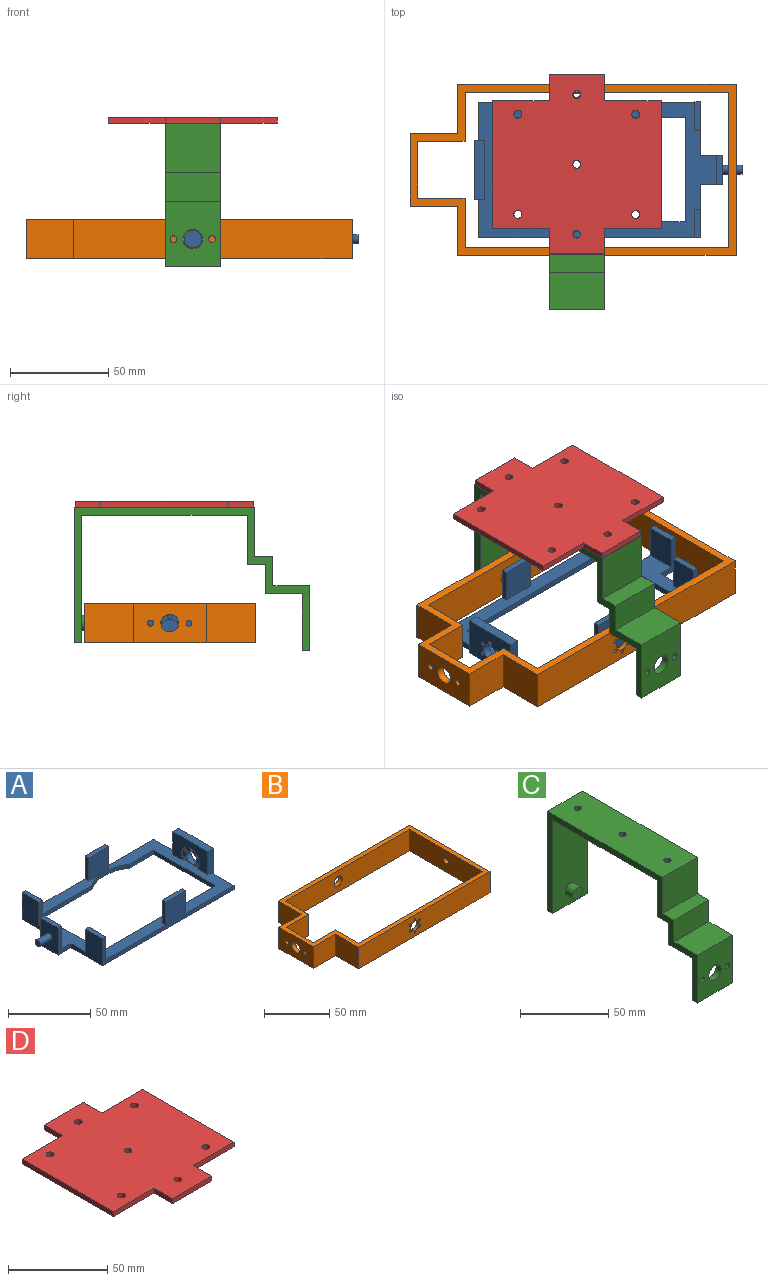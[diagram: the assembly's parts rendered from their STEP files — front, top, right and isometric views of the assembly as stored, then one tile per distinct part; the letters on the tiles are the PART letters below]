
ASSEMBLY  parts=4 mates=1
PART A: 48 faces, bbox 136x69x20 mm
  f0: cylinder r=4.5mm len=9mm, axis (1,0,0), area 113.1mm2, adj f43,f44
  f1: cylinder r=1mm len=4mm, axis (1,0,0), area 25.1mm2, adj f43,f44
  f2: cylinder r=1mm len=4mm, axis (1,0,0), area 25.1mm2, adj f43,f44
  f3: cylinder r=1mm len=4mm, axis (1,0,0), area 25.1mm2, adj f43,f44
  f4: cylinder r=1mm len=4mm, axis (1,0,0), area 25.1mm2, adj f43,f44
  f5: cylinder r=1mm len=4mm, axis (1,0,0), area 25.1mm2, adj f43,f44
  f6: plane 19.5x3mm, normal (1,0,0), area 58.5mm2, adj f7,f9,f24,f33
  f7: plane 121x69mm, normal (0,0,1), area 2401mm2, adj f6,f8,f9,f10,f11,f12,f13,f14
  f8: plane 27x20mm, normal (-1,0,0), area 327.5mm2, adj f7,f9,f18,f24,f36,f38
  f9: plane 113x20mm, normal (0,1,0), area 679mm2, adj f6,f7,f8,f16,f18,f22,f24,f32
  f10: plane 27x20mm, normal (-1,0,0), area 327.5mm2, adj f7,f11,f19,f24,f37,f39
  f11: plane 113x20mm, normal (0,-1,0), area 679mm2, adj f7,f10,f12,f17,f19,f23,f24,f31
  f12: plane 17x14.5mm, normal (1,0,0), area 246.5mm2, adj f7,f11,f19,f37
  f13: plane 17x17mm, normal (0,-1,0), area 289mm2, adj f7,f16,f32,f35
  f14: plane 30x17mm, normal (-1,0,0), area 352.1mm2, adj f7,f20,f30,f33,f45
  f15: plane 17x17mm, normal (0,1,0), area 289mm2, adj f7,f17,f31,f34
  f16: plane 17x3mm, normal (0,0,1), area 51mm2, adj f9,f13,f32,f35
  f17: plane 17x3mm, normal (0,0,1), area 51mm2, adj f11,f15,f31,f34
  f18: plane 14.5x3mm, normal (0,0,1), area 43.5mm2, adj f8,f9,f22,f36
  f19: plane 14.5x3mm, normal (0,0,1), area 43.5mm2, adj f10,f11,f12,f37
  f20: plane 30x5mm, normal (0,0,1), area 150mm2, adj f14,f30,f33,f43
  f21: plane 21.03x3mm, normal (0,-1,0), area 63.1mm2, adj f7,f24,f28,f29
  f22: plane 17x14.5mm, normal (1,0,0), area 246.5mm2, adj f7,f9,f18,f36
  f23: plane 19.5x3mm, normal (1,0,0), area 58.5mm2, adj f7,f11,f24,f30
  f24: plane 126x69mm, normal (0,0,-1), area 2772.5mm2, adj f6,f8,f9,f10,f11,f21,f23,f25
  f25: plane 44.03x3mm, normal (0,-1,0), area 132.1mm2, adj f7,f24,f26,f29
  f26: plane 53x3mm, normal (1,0,0), area 159mm2, adj f7,f24,f25,f27
  f27: plane 97x3mm, normal (0,1,0), area 291mm2, adj f7,f24,f26,f28
  f28: plane 53x3mm, normal (-1,0,0), area 159mm2, adj f7,f21,f24,f27
  f29: cylinder r=28mm len=31.94mm, axis (0,0,1), area 102mm2, adj f7,f21,f24,f25
  f30: plane 20x5mm, normal (0,-1,0), area 91mm2, adj f7,f14,f20,f23,f24,f43
  f31: plane 17x3mm, normal (1,0,0), area 51mm2, adj f7,f11,f15,f17
  f32: plane 17x3mm, normal (1,0,0), area 51mm2, adj f7,f9,f13,f16
  f33: plane 20x5mm, normal (0,1,0), area 91mm2, adj f6,f7,f14,f20,f24,f43
  f34: plane 17x3mm, normal (-1,0,0), area 51mm2, adj f7,f11,f15,f17
  f35: plane 17x3mm, normal (-1,0,0), area 51mm2, adj f7,f9,f13,f16
  f36: plane 17x3mm, normal (0,-1,0), area 51mm2, adj f7,f8,f18,f22
  f37: plane 17x3mm, normal (0,1,0), area 51mm2, adj f7,f10,f12,f19
  f38: plane 20x11mm, normal (0,1,0), area 84mm2, adj f7,f8,f24,f40,f41,f42
  f39: plane 20x11mm, normal (0,-1,0), area 84mm2, adj f7,f10,f24,f40,f41,f42
  f40: plane 20x15mm, normal (-1,0,0), area 283.4mm2, adj f24,f38,f39,f41,f46
  f41: plane 15x3mm, normal (0,0,1), area 45mm2, adj f38,f39,f40,f42
  f42: plane 17x15mm, normal (1,0,0), area 255mm2, adj f7,f38,f39,f41
  f43: plane 30x20mm, normal (1,0,0), area 520.7mm2, adj f0,f1,f2,f3,f4,f5,f20,f24
  f44: plane 15.38x12.19mm, normal (-1,0,0), area 78.6mm2, adj f0,f1,f2,f3,f4,f5,f7,f45
  f45: cylinder r=7.69mm len=15.38mm, axis (-1,0,0), area 33.8mm2, adj f7,f14,f44
  f46: cylinder r=2.3mm len=10mm, axis (1,0,0), area 144.5mm2, adj f40,f47
  f47: plane 4.6x4.6mm, normal (-1,0,0), area 16.6mm2, adj f46
PART B: 36 faces, bbox 166x87x20 mm
  f0: cylinder r=4.5mm len=9mm, axis (0,1,0), area 70.7mm2, adj f16,f34
  f1: cylinder r=1mm len=2.5mm, axis (0,-1,0), area 15.7mm2, adj f16,f34
  f2: cylinder r=1mm len=2.5mm, axis (0,-1,0), area 15.7mm2, adj f16,f34
  f3: cylinder r=1mm len=2.5mm, axis (0,-1,0), area 15.7mm2, adj f16,f34
  f4: cylinder r=1mm len=2.5mm, axis (0,-1,0), area 15.7mm2, adj f16,f34
  f5: cylinder r=1mm len=2.5mm, axis (0,-1,0), area 15.7mm2, adj f16,f34
  f6: cylinder r=1mm len=2.5mm, axis (0,-1,0), area 15.7mm2, adj f16,f34
  f7: plane 29x20mm, normal (1,0,0), area 473.9mm2, adj f17,f23,f25,f26,f29,f30,f33
  f8: cylinder r=1.5mm len=3mm, axis (1,0,0), area 23.6mm2, adj f10,f32
  f9: cylinder r=1.5mm len=3mm, axis (1,0,0), area 23.6mm2, adj f10,f31
  f10: plane 37x20mm, normal (-1,0,0), area 662.2mm2, adj f8,f9,f13,f14,f25,f26,f29
  f11: plane 142x20mm, normal (0,1,0), area 2776.4mm2, adj f12,f24,f25,f26,f28
  f12: plane 25x20mm, normal (-1,0,0), area 500mm2, adj f11,f13,f25,f26
  f13: plane 24x20mm, normal (0,1,0), area 480mm2, adj f10,f12,f25,f26
  f14: plane 24x20mm, normal (0,-1,0), area 480mm2, adj f10,f15,f25,f26
  f15: plane 25x20mm, normal (-1,0,0), area 500mm2, adj f14,f16,f25,f26
  f16: plane 142x20mm, normal (0,-1,0), area 2757.5mm2, adj f0,f1,f2,f3,f4,f5,f6,f15
  f17: plane 24x20mm, normal (0,-1,0), area 480mm2, adj f7,f18,f25,f26
  f18: plane 25x20mm, normal (1,0,0), area 500mm2, adj f17,f19,f25,f26
  f19: plane 134x20mm, normal (0,-1,0), area 2616.4mm2, adj f18,f20,f25,f26,f28
  f20: plane 79x20mm, normal (-1,0,0), area 1560.4mm2, adj f19,f21,f25,f26,f27
  f21: plane 134x20mm, normal (0,1,0), area 2483.9mm2, adj f20,f22,f25,f26,f35
  f22: plane 25x20mm, normal (1,0,0), area 500mm2, adj f21,f23,f25,f26
  f23: plane 24x20mm, normal (0,1,0), area 480mm2, adj f7,f22,f25,f26
  f24: plane 87x20mm, normal (1,0,0), area 1720.4mm2, adj f11,f16,f25,f26,f27
  f25: plane 166x87mm, normal (0,0,1), area 1960mm2, adj f7,f10,f11,f12,f13,f14,f15,f16
  f26: plane 166x87mm, normal (0,0,-1), area 1960mm2, adj f7,f10,f11,f12,f13,f14,f15,f16
  f27: cylinder r=2.5mm len=5mm, axis (1,0,0), area 62.8mm2, adj f20,f24
  f28: cylinder r=4.5mm len=9mm, axis (0,1,0), area 113.1mm2, adj f11,f19
  f29: cylinder r=4.5mm len=9mm, axis (1,0,0), area 113.1mm2, adj f7,f10
  f30: cylinder r=2.6mm len=5.2mm, axis (1,0,0), area 24.5mm2, adj f7,f31
  f31: plane 5.2x5.2mm, normal (1,0,0), area 14.2mm2, adj f9,f30
  f32: plane 5.2x5.2mm, normal (1,0,0), area 14.2mm2, adj f8,f33
  f33: cylinder r=2.6mm len=5.2mm, axis (1,0,0), area 24.5mm2, adj f7,f32
  f34: plane 15.8x15.8mm, normal (0,1,0), area 113.6mm2, adj f0,f1,f2,f3,f4,f5,f6,f35
  f35: cylinder r=7.9mm len=15.8mm, axis (0,1,0), area 74.5mm2, adj f21,f34
PART C: 26 faces, bbox 28x120x73 mm
  f0: plane 84x28mm, normal (0,0,-1), area 2314.3mm2, adj f7,f8,f16,f17,f23,f24,f25
  f1: plane 92x28mm, normal (0,0,1), area 2538.3mm2, adj f10,f11,f16,f17,f23,f24,f25
  f2: plane 33x28mm, normal (0,-1,0), area 826.2mm2, adj f14,f15,f16,f17,f20,f21,f22
  f3: plane 29x28mm, normal (0,1,0), area 714.2mm2, adj f4,f15,f16,f17,f20,f21,f22
  f4: plane 28x18.81mm, normal (0,0,-1), area 526.7mm2, adj f3,f5,f16,f17
  f5: plane 28x15mm, normal (0,1,0), area 420mm2, adj f4,f6,f16,f17
  f6: plane 28x9.19mm, normal (0,0,-1), area 257.3mm2, adj f5,f7,f16,f17
  f7: plane 28x25mm, normal (0,1,0), area 700mm2, adj f0,f6,f16,f17
  f8: plane 65x28mm, normal (0,-1,0), area 1769.7mm2, adj f0,f9,f16,f17,f18
  f9: plane 28x4mm, normal (0,0,-1), area 112mm2, adj f8,f10,f16,f17
  f10: plane 69x28mm, normal (0,1,0), area 1932mm2, adj f1,f9,f16,f17
  f11: plane 28x25mm, normal (0,-1,0), area 700mm2, adj f1,f12,f16,f17
  f12: plane 28x9.19mm, normal (0,0,1), area 257.3mm2, adj f11,f13,f16,f17
  f13: plane 28x15mm, normal (0,-1,0), area 420mm2, adj f12,f14,f16,f17
  f14: plane 28x18.81mm, normal (0,0,1), area 526.7mm2, adj f2,f13,f16,f17
  f15: plane 28x4mm, normal (0,0,-1), area 112mm2, adj f2,f3,f16,f17
  f16: plane 120x73mm, normal (1,0,0), area 1016mm2, adj f0,f1,f2,f3,f4,f5,f6,f7
  f17: plane 120x73mm, normal (-1,0,0), area 1016mm2, adj f0,f1,f2,f3,f4,f5,f6,f7
  f18: cylinder r=4mm len=8mm, axis (0,1,0), area 150.8mm2, adj f8,f19
  f19: plane 8x8mm, normal (0,-1,0), area 50.3mm2, adj f18
  f20: cylinder r=5mm len=10mm, axis (0,-1,0), area 125.7mm2, adj f2,f3
  f21: cylinder r=1.75mm len=4mm, axis (0,-1,0), area 44mm2, adj f2,f3
  f22: cylinder r=1.75mm len=4mm, axis (0,-1,0), area 44mm2, adj f2,f3
  f23: cylinder r=2mm len=4mm, axis (0,0,1), area 50.3mm2, adj f0,f1
  f24: cylinder r=2mm len=4mm, axis (0,0,1), area 50.3mm2, adj f0,f1
  f25: cylinder r=2mm len=4mm, axis (0,0,1), area 50.3mm2, adj f0,f1
PART D: 21 faces, bbox 86x91x3 mm
  f0: plane 28x3mm, normal (0,1,0), area 84mm2, adj f11,f12,f18,f19
  f1: plane 65x3mm, normal (-1,0,0), area 195mm2, adj f11,f12,f16,f17
  f2: plane 28x3mm, normal (0,-1,0), area 84mm2, adj f11,f12,f14,f15
  f3: plane 65x3mm, normal (1,0,0), area 195mm2, adj f11,f12,f13,f20
  f4: cylinder r=2mm len=4mm, axis (0,0,-1), area 37.7mm2, adj f11,f12
  f5: cylinder r=2mm len=4mm, axis (0,0,-1), area 37.7mm2, adj f11,f12
  f6: cylinder r=2mm len=4mm, axis (0,0,-1), area 37.7mm2, adj f11,f12
  f7: cylinder r=2mm len=4mm, axis (0,0,-1), area 37.7mm2, adj f11,f12
  f8: cylinder r=2mm len=4mm, axis (0,0,-1), area 37.7mm2, adj f11,f12
  f9: cylinder r=2mm len=4mm, axis (0,0,-1), area 37.7mm2, adj f11,f12
  f10: cylinder r=2mm len=4mm, axis (0,0,-1), area 37.7mm2, adj f11,f12
  f11: plane 91x86mm, normal (0,0,1), area 6230mm2, adj f0,f1,f2,f3,f4,f5,f6,f7
  f12: plane 91x86mm, normal (0,0,-1), area 6230mm2, adj f0,f1,f2,f3,f4,f5,f6,f7
  f13: plane 29x3mm, normal (0,-1,0), area 87mm2, adj f3,f11,f12,f14
  f14: plane 13x3mm, normal (1,0,0), area 39mm2, adj f2,f11,f12,f13
  f15: plane 13x3mm, normal (-1,0,0), area 39mm2, adj f2,f11,f12,f16
  f16: plane 29x3mm, normal (0,-1,0), area 87mm2, adj f1,f11,f12,f15
  f17: plane 29x3mm, normal (0,1,0), area 87mm2, adj f1,f11,f12,f18
  f18: plane 13x3mm, normal (-1,0,0), area 39mm2, adj f0,f11,f12,f17
  f19: plane 13x3mm, normal (1,0,0), area 39mm2, adj f0,f11,f12,f20
  f20: plane 29x3mm, normal (0,1,0), area 87mm2, adj f3,f11,f12,f19
PLACE A rot(axis=(0,0,1),180deg) t=(60.54,9.6,-6.83)mm
PLACE B t=(54.04,9.6,-6.83)mm
PLACE C t=(53.93,-14.36,22.55)mm
PLACE D t=(53.93,12.26,62.17)mm
MATE parallel D.f9 <-> C.f23  axis (0,0,-1) through (53.93,12.26,62.17)mm
